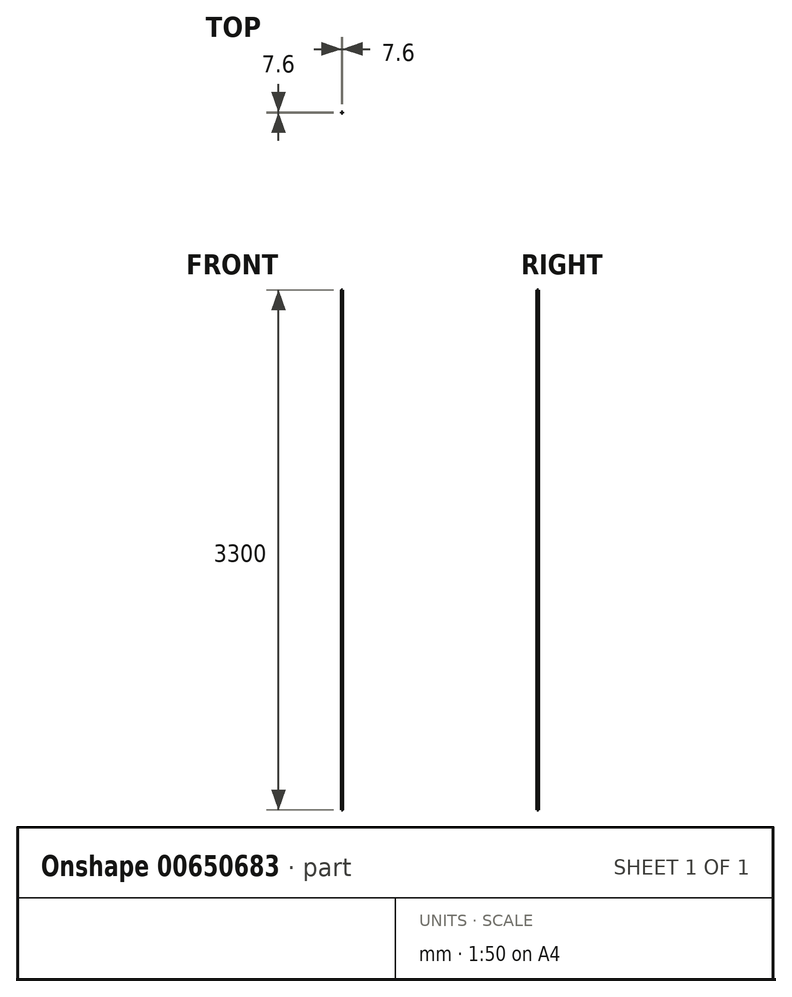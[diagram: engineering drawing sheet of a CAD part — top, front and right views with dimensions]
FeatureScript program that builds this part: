
annotation { "Feature Type Name" : "Feature", "Feature Type Description" : "" }
export const myFeature = defineFeature(function(context is Context, id is Id, definition is map)
    precondition{}
    {
        {
            var Q0;
            Q0=qCreatedBy(makeId("Top.planeOp"),FACE);
            var sketch = newSketch(context, id + "F0", { "sketchPlane" : qUnion([Q0])});
            skCircle(sketch, "E0", {"center": v(-40.08, 21.5) * mm, "radius": 3.8 * mm});
            skSolve(sketch);
        }
        {
            var Q0;
            Q0=makeQuery(id+"F0.imprint","IMPRINT",FACE,{"disambiguationData":[TD([[makeQuery(id+"F0.imprint","IMPRINT",EDGE,{"derivedFrom":sQuery(id+"F0.wireOp",EDGE,"E0")}),1.0]])]});
            extrude(context, id + "F1", {"entities" : qUnion([Q0]), "depth" : 3300 * mm, "offsetDistance" : 25 * mm});
        }
    });
